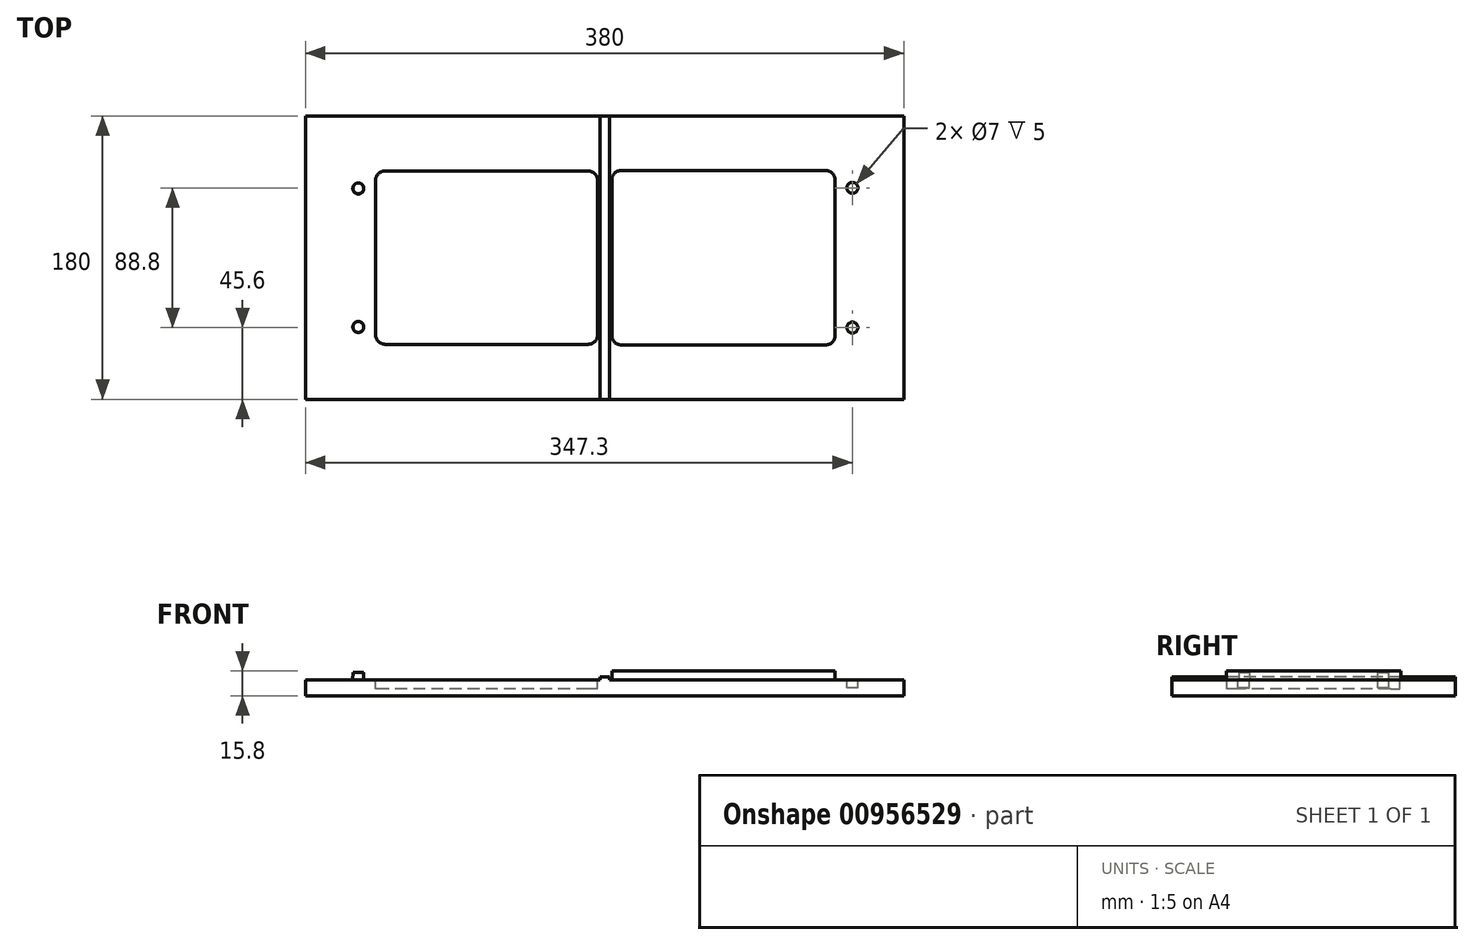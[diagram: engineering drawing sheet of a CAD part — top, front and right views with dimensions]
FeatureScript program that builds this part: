
annotation { "Feature Type Name" : "Feature", "Feature Type Description" : "" }
export const myFeature = defineFeature(function(context is Context, id is Id, definition is map)
    precondition{}
    {
        {
            var Q0;
            Q0=qCreatedBy(makeId("Top.planeOp"),FACE);
            var sketch = newSketch(context, id + "F0", { "sketchPlane" : qUnion([Q0])});
            skLineSegment(sketch, "E0.bottom", {"start": v(190, 90) * mm, "end": v(-190, 90) * mm});
            skLineSegment(sketch, "E0.top", {"start": v(190, -90) * mm, "end": v(-190, -90) * mm});
            skLineSegment(sketch, "E0.left", {"start": v(190, 90) * mm, "end": v(190, -90) * mm});
            skLineSegment(sketch, "E0.right", {"start": v(-190, 90) * mm, "end": v(-190, -90) * mm});
            skPoint(sketch, "E0.middle", {"position": v(0, 0) * mm});
            skSolve(sketch);
        }
        {
            var Q0;
            Q0 = qSketchRegion(id + "F0", true);
            extrude(context, id + "F1", {"entities" : qUnion([Q0]), "depth" : 10 * mm, "offsetDistance" : 25 * mm});
        }
        {
            var Q0;
            Q0=makeQuery(id+"F1.opExtrude","CAP_FACE",FACE,{"disambiguationData":[OSD([sQuery(id+"F0.wireOp",EDGE,"E0.bottom"),sQuery(id+"F0.wireOp",EDGE,"E0.top"),sQuery(id+"F0.wireOp",EDGE,"E0.left"),sQuery(id+"F0.wireOp",EDGE,"E0.right")])],"isStart":false});
            var sketch = newSketch(context, id + "F2", { "sketchPlane" : qUnion([Q0])});
            skLineSegment(sketch, "E1.bottom", {"start": v(3, 90) * mm, "end": v(-3, 90) * mm});
            skLineSegment(sketch, "E1.top", {"start": v(3, -90) * mm, "end": v(-3, -90) * mm});
            skLineSegment(sketch, "E1.left", {"start": v(3, 90) * mm, "end": v(3, -90) * mm});
            skLineSegment(sketch, "E1.right", {"start": v(-3, 90) * mm, "end": v(-3, -90) * mm});
            skPoint(sketch, "E1.middle", {"position": v(0, 0) * mm});
            skSolve(sketch);
        }
        {
            var Q0;
            Q0 = qSketchRegion(id + "F2", true);
            extrude(context, id + "F3", {"entities" : qUnion([Q0]), "operationType" : NewBodyOperationType.ADD, "depth" : 2 * mm, "offsetDistance" : 25 * mm});
        }
        {
            var Q0;
            {var subQ0=sQuery(id+"F0.wireOp",EDGE,"E0.top");var subQ1=sQuery(id+"F0.wireOp",EDGE,"E0.right");var subQ2=sQuery(id+"F0.wireOp",EDGE,"E0.bottom");Q0=makeQuery(id+"F3.boolean.opBoolean","SPLIT",FACE,{"disambiguationData":[TD([makeQuery(id+"F1.opExtrude","SWEPT_FACE",FACE,{"disambiguationData":[OSD([subQ1])]})])],"derivedFrom":makeQuery(id+"F1.opExtrude","CAP_FACE",FACE,{"disambiguationData":[OSD([subQ2,subQ0,sQuery(id+"F0.wireOp",EDGE,"E0.left"),subQ1])],"isStart":false})});}
            var sketch = newSketch(context, id + "F4", { "sketchPlane" : qUnion([Q0])});
            skLineSegment(sketch, "E2.bottom", {"start": v(-10.5, 55) * mm, "end": v(-139.5, 55) * mm});
            skLineSegment(sketch, "E2.top", {"start": v(-10.5, -55) * mm, "end": v(-139.5, -55) * mm});
            skLineSegment(sketch, "E2.left", {"start": v(-4.5, 49) * mm, "end": v(-4.5, -49) * mm});
            skLineSegment(sketch, "E2.right", {"start": v(-145.5, 49) * mm, "end": v(-145.5, -49) * mm});
            skPoint(sketch, "E2.middle", {"position": v(-75, 0) * mm});
            skPoint(sketch, "E3.visualSharp", {"position": v(-145.5, 55) * mm});
            skArc(sketch, "E3.filletArc", {"start": v(-139.5, 55) * mm, "mid": v(-143.74, 53.24) * mm, "end": v(-145.5, 49) * mm});
            skPoint(sketch, "E4.visualSharp", {"position": v(-4.5, 55) * mm});
            skArc(sketch, "E4.filletArc", {"start": v(-4.5, 49) * mm, "mid": v(-6.26, 53.24) * mm, "end": v(-10.5, 55) * mm});
            skPoint(sketch, "E5.visualSharp", {"position": v(-4.5, -55) * mm});
            skArc(sketch, "E5.filletArc", {"start": v(-10.5, -55) * mm, "mid": v(-6.26, -53.24) * mm, "end": v(-4.5, -49) * mm});
            skPoint(sketch, "E6.visualSharp", {"position": v(-145.5, -55) * mm});
            skArc(sketch, "E6.filletArc", {"start": v(-145.5, -49) * mm, "mid": v(-143.74, -53.24) * mm, "end": v(-139.5, -55) * mm});
            skSolve(sketch);
        }
        {
            var Q0;
            Q0 = qSketchRegion(id + "F4", true);
            extrude(context, id + "F5", {"entities" : qUnion([Q0]), "operationType" : NewBodyOperationType.REMOVE, "oppositeDirection" : true, "depth" : 5.6 * mm, "offsetDistance" : 25 * mm});
        }
        {
            var Q0;
            {var subQ0=sQuery(id+"F0.wireOp",EDGE,"E0.left");var subQ1=sQuery(id+"F0.wireOp",EDGE,"E0.top");var subQ2=sQuery(id+"F0.wireOp",EDGE,"E0.bottom");Q0=makeQuery(id+"F3.boolean.opBoolean","SPLIT",FACE,{"disambiguationData":[TD([makeQuery(id+"F1.opExtrude","SWEPT_FACE",FACE,{"disambiguationData":[OSD([subQ0])]})])],"derivedFrom":makeQuery(id+"F1.opExtrude","CAP_FACE",FACE,{"disambiguationData":[OSD([subQ2,subQ1,subQ0,sQuery(id+"F0.wireOp",EDGE,"E0.right")])],"isStart":false})});}
            var sketch = newSketch(context, id + "F6", { "sketchPlane" : qUnion([Q0])});
            skLineSegment(sketch, "E7.bottom", {"start": v(10.5, 55.4) * mm, "end": v(140.3, 55.4) * mm});
            skLineSegment(sketch, "E7.top", {"start": v(10.5, -55.4) * mm, "end": v(140.3, -55.4) * mm});
            skLineSegment(sketch, "E7.left", {"start": v(4.5, 49.4) * mm, "end": v(4.5, -49.4) * mm});
            skLineSegment(sketch, "E7.right", {"start": v(146.3, 49.4) * mm, "end": v(146.3, -49.4) * mm});
            skPoint(sketch, "E7.middle", {"position": v(75.4, 0) * mm});
            skPoint(sketch, "E7.middle.positionSnap0", {"position": v(3, 0) * mm});
            skPoint(sketch, "E7.centerSnap0", {"position": v(3, 0) * mm});
            skPoint(sketch, "E8.visualSharp", {"position": v(4.5, 55.4) * mm});
            skArc(sketch, "E8.filletArc", {"start": v(10.5, 55.4) * mm, "mid": v(6.26, 53.64) * mm, "end": v(4.5, 49.4) * mm});
            skPoint(sketch, "E9.visualSharp", {"position": v(146.3, 55.4) * mm});
            skArc(sketch, "E9.filletArc", {"start": v(146.3, 49.4) * mm, "mid": v(144.54, 53.64) * mm, "end": v(140.3, 55.4) * mm});
            skPoint(sketch, "E10.visualSharp", {"position": v(146.3, -55.4) * mm});
            skArc(sketch, "E10.filletArc", {"start": v(140.3, -55.4) * mm, "mid": v(144.54, -53.64) * mm, "end": v(146.3, -49.4) * mm});
            skPoint(sketch, "E11.visualSharp", {"position": v(4.5, -55.4) * mm});
            skArc(sketch, "E11.filletArc", {"start": v(4.5, -49.4) * mm, "mid": v(6.26, -53.64) * mm, "end": v(10.5, -55.4) * mm});
            skSolve(sketch);
        }
        {
            var Q0;
            Q0 = qSketchRegion(id + "F6", true);
            extrude(context, id + "F7", {"entities" : qUnion([Q0]), "operationType" : NewBodyOperationType.ADD, "depth" : 5.8 * mm, "offsetDistance" : 25 * mm});
        }
        {
            var Q0;
            {var subQ0=sQuery(id+"F0.wireOp",EDGE,"E0.top");var subQ1=sQuery(id+"F0.wireOp",EDGE,"E0.right");var subQ2=sQuery(id+"F0.wireOp",EDGE,"E0.bottom");Q0=makeQuery(id+"F3.boolean.opBoolean","SPLIT",FACE,{"disambiguationData":[TD([makeQuery(id+"F1.opExtrude","SWEPT_FACE",FACE,{"disambiguationData":[OSD([subQ1])]})])],"derivedFrom":makeQuery(id+"F1.opExtrude","CAP_FACE",FACE,{"disambiguationData":[OSD([subQ2,subQ0,sQuery(id+"F0.wireOp",EDGE,"E0.left"),subQ1])],"isStart":false})});}
            var sketch = newSketch(context, id + "F8", { "sketchPlane" : qUnion([Q0])});
            skCircle(sketch, "E12", {"center": v(-156.5, 44) * mm, "radius": 3.5 * mm});
            skLineSegment(sketch, "E13", {"start": v(-218.9, 0) * mm, "end": v(0, 0) * mm, "construction": true});
            skCircle(sketch, "E14.MirrorC", {"center": v(-156.5, -44) * mm, "radius": 3.5 * mm});
            skSolve(sketch);
        }
        {
            var Q0;
            Q0 = qSketchRegion(id + "F8", true);
            extrude(context, id + "F9", {"entities" : qUnion([Q0]), "operationType" : NewBodyOperationType.ADD, "depth" : 5 * mm, "offsetDistance" : 25 * mm, "hasDraft" : true, "draftAngle" : 1 * degree, "draftPullDirection" : true});
        }
        {
            var Q0;
            {var subQ0=sQuery(id+"F0.wireOp",EDGE,"E0.left");var subQ1=sQuery(id+"F0.wireOp",EDGE,"E0.top");var subQ2=sQuery(id+"F0.wireOp",EDGE,"E0.bottom");Q0=makeQuery(id+"F3.boolean.opBoolean","SPLIT",FACE,{"disambiguationData":[TD([makeQuery(id+"F1.opExtrude","SWEPT_FACE",FACE,{"disambiguationData":[OSD([subQ0])]})])],"derivedFrom":makeQuery(id+"F1.opExtrude","CAP_FACE",FACE,{"disambiguationData":[OSD([subQ2,subQ1,subQ0,sQuery(id+"F0.wireOp",EDGE,"E0.right")])],"isStart":false})});}
            var sketch = newSketch(context, id + "F10", { "sketchPlane" : qUnion([Q0])});
            skCircle(sketch, "E15", {"center": v(157.3, 44.4) * mm, "radius": 3.5 * mm});
            skLineSegment(sketch, "E16", {"start": v(0, 0) * mm, "end": v(222.36, 0) * mm, "construction": true});
            skCircle(sketch, "E17.MirrorC", {"center": v(157.3, -44.4) * mm, "radius": 3.5 * mm});
            skSolve(sketch);
        }
        {
            var Q0;
            Q0 = qSketchRegion(id + "F10", true);
            extrude(context, id + "F11", {"entities" : qUnion([Q0]), "operationType" : NewBodyOperationType.REMOVE, "oppositeDirection" : true, "depth" : 5 * mm, "offsetDistance" : 25 * mm});
        }
    });
